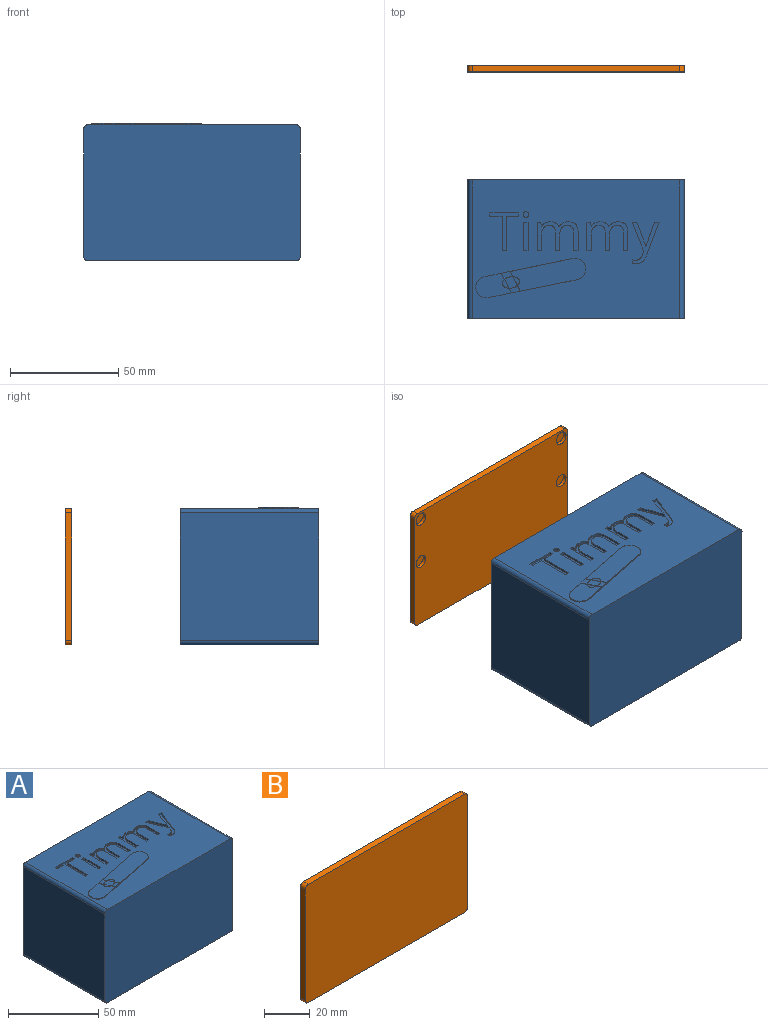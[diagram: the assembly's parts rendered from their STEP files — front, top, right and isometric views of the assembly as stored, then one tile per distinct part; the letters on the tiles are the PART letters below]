
ASSEMBLY  parts=2 mates=1
PART A: 152 faces, bbox 100x64x63.7 mm
  f0: plane 5.34x3.69mm, normal (0,0,1), area 10.9mm2, adj f140,f145,f146,f149
  f1: plane 96x64mm, normal (0,0,1), area 5297.7mm2, adj f2,f7,f37,f38,f39,f40,f41,f42
  f2: plane 100x63mm, normal (0,1,0), area 2285.3mm2, adj f1,f3,f4,f6,f8,f9,f10,f11
  f3: plane 47.5x22.2mm, normal (0,0,-1), area 1054.5mm2, adj f2,f5,f14,f18
  f4: plane 47.5x22.2mm, normal (0,0,1), area 1054.5mm2, adj f2,f5,f14,f18
  f5: cylinder r=15mm len=30mm, axis (1,0,0), area 1046.2mm2, adj f3,f4,f14,f18
  f6: plane 64x59mm, normal (-1,0,0), area 3776mm2, adj f2,f7,f135,f137
  f7: plane 100x63mm, normal (0,-1,0), area 6296.6mm2, adj f1,f6,f8,f9,f135,f136,f137,f138
  f8: plane 64x59mm, normal (1,0,0), area 3776mm2, adj f2,f7,f136,f138
  f9: plane 96x64mm, normal (0,0,-1), area 6144mm2, adj f2,f7,f135,f136
  f10: plane 62.5x30mm, normal (1,0,0), area 1778.4mm2, adj f2,f11,f12,f13
  f11: plane 66.5x47.5mm, normal (0,0,-1), area 3158.8mm2, adj f2,f10,f13,f16
  f12: plane 66.5x47.5mm, normal (0,0,1), area 3158.8mm2, adj f2,f10,f13,f16
  f13: cylinder r=15mm len=66.5mm, axis (1,0,0), area 3133.7mm2, adj f10,f11,f12,f16
  f14: plane 62.5x30mm, normal (-1,0,0), area 1778.4mm2, adj f2,f3,f4,f5
  f15: plane 63x7.8mm, normal (0,0,-1), area 491.4mm2, adj f2,f16,f18,f19
  f16: plane 63x32mm, normal (1,0,0), area 237.6mm2, adj f2,f11,f12,f13,f15,f17,f19
  f17: plane 63x7.8mm, normal (0,0,1), area 491.4mm2, adj f2,f16,f18,f19
  f18: plane 63x32mm, normal (-1,0,0), area 237.6mm2, adj f2,f3,f4,f5,f15,f17,f19
  f19: plane 32x7.8mm, normal (0,1,0), area 249.6mm2, adj f15,f16,f17,f18
  f20: plane 73x42mm, normal (0,0,1), area 2851mm2, adj f2,f21,f23,f24,f25,f27,f28
  f21: plane 42x13mm, normal (1,0,0), area 546mm2, adj f2,f20,f22,f24
  f22: plane 73x42mm, normal (0,0,-1), area 3066mm2, adj f2,f21,f23,f24
  f23: plane 42x13mm, normal (-1,0,0), area 546mm2, adj f2,f20,f22,f24
  f24: plane 73x13mm, normal (0,1,0), area 949mm2, adj f20,f21,f22,f23
  f25: plane 25x3mm, normal (-1,0,0), area 75mm2, adj f2,f20,f26,f28
  f26: plane 25x8.6mm, normal (0,0,1), area 215mm2, adj f2,f25,f27,f28
  f27: plane 25x3mm, normal (1,0,0), area 75mm2, adj f2,f20,f26,f28
  f28: plane 8.6x3mm, normal (0,1,0), area 25.8mm2, adj f20,f25,f26,f27
  f29: cylinder r=3.17mm len=6.33mm, axis (0,1,0), area 32mm2, adj f2,f30
  f30: plane 6.33x6.33mm, normal (0,1,0), area 31.5mm2, adj f29
  f31: cylinder r=3.17mm len=6.33mm, axis (0,1,0), area 32mm2, adj f2,f32
  f32: plane 6.33x6.33mm, normal (0,1,0), area 31.5mm2, adj f31
  f33: cylinder r=3.17mm len=6.33mm, axis (0,1,0), area 32mm2, adj f2,f34
  f34: plane 6.33x6.33mm, normal (0,1,0), area 31.5mm2, adj f33
  f35: cylinder r=3.17mm len=6.33mm, axis (0,1,0), area 32mm2, adj f2,f36
  f36: plane 6.33x6.33mm, normal (0,1,0), area 31.5mm2, adj f35
  f37: plane 2.15x1mm, normal (0,-1,0), area 2.2mm2, adj f1,f38,f52,f53
  f38: plane 13.31x5.34mm, normal (0.93,0.37,0), area 14.3mm2, adj f1,f37,f39,f53
  f39: plane 1.88x1mm, normal (0.93,-0.37,0), area 2mm2, adj f1,f38,f40,f53
  f40: extruded ~2.95x2.32mm, area 4mm2, adj f1,f39,f41,f53
  f41: extruded ~1.48x1mm, area 1.5mm2, adj f1,f40,f42,f53
  f42: plane 1.6x1mm, normal (1,0,0), area 1.6mm2, adj f1,f41,f43,f53
  f43: extruded ~1.81x1mm, area 1.8mm2, adj f1,f42,f44,f53
  f44: extruded ~2.77x1mm, area 3mm2, adj f1,f43,f45,f53
  f45: extruded ~3.17x1.98mm, area 3.8mm2, adj f1,f44,f46,f53
  f46: plane 15.07x5.69mm, normal (-0.94,0.35,0), area 16.1mm2, adj f1,f45,f47,f53
  f47: plane 2.15x1mm, normal (0,-1,0), area 2.1mm2, adj f1,f46,f48,f53
  f48: extruded ~9.17x3.28mm, area 9.7mm2, adj f1,f47,f49,f53
  f49: extruded ~2.11x1mm, area 2.2mm2, adj f1,f48,f50,f53
  f50: plane 1x0.1mm, normal (0,-1,0), area 0.1mm2, adj f1,f49,f51,f53
  f51: extruded ~3.73x1.18mm, area 3.9mm2, adj f1,f50,f52,f53
  f52: plane 7.55x2.9mm, normal (-0.93,-0.36,0), area 8.1mm2, adj f1,f37,f51,f53
  f53: plane 19.18x12.42mm, normal (0,0,1), area 68mm2, adj f37,f38,f39,f40,f41,f42,f43,f44
  f54: plane 8.61x1mm, normal (1,0,0), area 8.6mm2, adj f1,f55,f81,f82
  f55: plane 2x1mm, normal (0,1,0), area 2mm2, adj f1,f54,f56,f82
  f56: plane 8.63x1mm, normal (-1,0,0), area 8.6mm2, adj f1,f55,f57,f82
  f57: extruded ~3.69x1.12mm, area 4mm2, adj f1,f56,f58,f82
  f58: extruded ~3.36x1.15mm, area 3.7mm2, adj f1,f57,f59,f82
  f59: extruded ~2.56x1mm, area 2.7mm2, adj f1,f58,f60,f82
  f60: extruded ~1.71x1.64mm, area 2.4mm2, adj f1,f59,f61,f82
  f61: plane 1x0.1mm, normal (0,-1,0), area 0.1mm2, adj f1,f60,f62,f82
  f62: extruded ~4.06x2.25mm, area 5mm2, adj f1,f61,f63,f82
  f63: extruded ~2.31x1mm, area 2.4mm2, adj f1,f62,f64,f82
  f64: extruded ~1.6x1.51mm, area 2.2mm2, adj f1,f63,f65,f82
  f65: plane 1x0.1mm, normal (0,-1,0), area 0.1mm2, adj f1,f64,f66,f82
  f66: plane 1.81x1mm, normal (-0.98,-0.18,0), area 1.8mm2, adj f1,f65,f67,f82
  f67: plane 1.63x1mm, normal (0,-1,0), area 1.6mm2, adj f1,f66,f68,f82
  f68: plane 13.24x1mm, normal (1,0,0), area 13.2mm2, adj f1,f67,f69,f82
  f69: plane 2.01x1mm, normal (0,1,0), area 2mm2, adj f1,f68,f70,f82
  f70: plane 6.95x1mm, normal (-1,0,0), area 6.9mm2, adj f1,f69,f71,f82
  f71: extruded ~3.7x1mm, area 3.9mm2, adj f1,f70,f72,f82
  f72: extruded ~2.76x1.13mm, area 3.1mm2, adj f1,f71,f73,f82
  f73: extruded ~2.11x1mm, area 2.3mm2, adj f1,f72,f74,f82
  f74: extruded ~2.38x1mm, area 2.5mm2, adj f1,f73,f75,f82
  f75: plane 8.61x1mm, normal (1,0,0), area 8.6mm2, adj f1,f74,f76,f82
  f76: plane 2.01x1mm, normal (0,1,0), area 2mm2, adj f1,f75,f77,f82
  f77: plane 7.39x1mm, normal (-1,0,0), area 7.4mm2, adj f1,f76,f78,f82
  f78: extruded ~3.31x1mm, area 3.5mm2, adj f1,f77,f79,f82
  f79: extruded ~2.77x1.07mm, area 3.1mm2, adj f1,f78,f80,f82
  f80: extruded ~2.1x1mm, area 2.3mm2, adj f1,f79,f81,f82
  f81: extruded ~2.38x1mm, area 2.5mm2, adj f1,f54,f80,f82
  f82: plane 18.88x13.48mm, normal (0,0,1), area 99.3mm2, adj f54,f55,f56,f57,f58,f59,f60,f61
  f83: plane 8.61x1mm, normal (1,0,0), area 8.6mm2, adj f1,f84,f110,f111
  f84: plane 2x1mm, normal (0,1,0), area 2mm2, adj f1,f83,f85,f111
  f85: plane 8.63x1mm, normal (-1,0,0), area 8.6mm2, adj f1,f84,f86,f111
  f86: extruded ~3.69x1.12mm, area 4mm2, adj f1,f85,f87,f111
  f87: extruded ~3.36x1.15mm, area 3.7mm2, adj f1,f86,f88,f111
  f88: extruded ~2.56x1mm, area 2.7mm2, adj f1,f87,f89,f111
  f89: extruded ~1.71x1.64mm, area 2.4mm2, adj f1,f88,f90,f111
  f90: plane 1x0.1mm, normal (0,-1,0), area 0.1mm2, adj f1,f89,f91,f111
  f91: extruded ~4.06x2.25mm, area 5mm2, adj f1,f90,f92,f111
  f92: extruded ~2.31x1mm, area 2.4mm2, adj f1,f91,f93,f111
  f93: extruded ~1.6x1.51mm, area 2.2mm2, adj f1,f92,f94,f111
  f94: plane 1x0.1mm, normal (0,-1,0), area 0.1mm2, adj f1,f93,f95,f111
  f95: plane 1.81x1mm, normal (-0.98,-0.18,0), area 1.8mm2, adj f1,f94,f96,f111
  f96: plane 1.63x1mm, normal (0,-1,0), area 1.6mm2, adj f1,f95,f97,f111
  f97: plane 13.24x1mm, normal (1,0,0), area 13.2mm2, adj f1,f96,f98,f111
  f98: plane 2.01x1mm, normal (0,1,0), area 2mm2, adj f1,f97,f99,f111
  f99: plane 6.95x1mm, normal (-1,0,0), area 6.9mm2, adj f1,f98,f100,f111
  f100: extruded ~3.7x1mm, area 3.9mm2, adj f1,f99,f101,f111
  f101: extruded ~2.76x1.13mm, area 3.1mm2, adj f1,f100,f102,f111
  f102: extruded ~2.11x1mm, area 2.3mm2, adj f1,f101,f103,f111
  f103: extruded ~2.38x1mm, area 2.5mm2, adj f1,f102,f104,f111
  f104: plane 8.61x1mm, normal (1,0,0), area 8.6mm2, adj f1,f103,f105,f111
  f105: plane 2.01x1mm, normal (0,1,0), area 2mm2, adj f1,f104,f106,f111
  f106: plane 7.39x1mm, normal (-1,0,0), area 7.4mm2, adj f1,f105,f107,f111
  f107: extruded ~3.31x1mm, area 3.5mm2, adj f1,f106,f108,f111
  f108: extruded ~2.77x1.07mm, area 3.1mm2, adj f1,f107,f109,f111
  f109: extruded ~2.1x1mm, area 2.3mm2, adj f1,f108,f110,f111
  f110: extruded ~2.38x1mm, area 2.5mm2, adj f1,f83,f109,f111
  f111: plane 18.88x13.48mm, normal (0,0,1), area 99.3mm2, adj f83,f84,f85,f86,f87,f88,f89,f90
  f112: extruded ~1.01x1mm, area 1.1mm2, adj f1,f113,f119,f120
  f113: extruded ~1.01x1mm, area 1.1mm2, adj f1,f112,f114,f120
  f114: extruded ~1x0.85mm, area 0.9mm2, adj f1,f113,f115,f120
  f115: extruded ~1x0.83mm, area 0.9mm2, adj f1,f114,f116,f120
  f116: extruded ~1.01x1mm, area 1.1mm2, adj f1,f115,f117,f120
  f117: extruded ~1x1mm, area 1.1mm2, adj f1,f116,f118,f120
  f118: extruded ~1x0.83mm, area 0.9mm2, adj f1,f117,f119,f120
  f119: extruded ~1x0.85mm, area 0.9mm2, adj f1,f112,f118,f120
  f120: plane 2.67x2.37mm, normal (0,0,1), area 5.2mm2, adj f112,f113,f114,f115,f116,f117,f118,f119
  f121: plane 2.01x1mm, normal (0,1,0), area 2mm2, adj f1,f122,f124,f125
  f122: plane 13.24x1mm, normal (-1,0,0), area 13.2mm2, adj f1,f121,f123,f125
  f123: plane 2.01x1mm, normal (0,-1,0), area 2mm2, adj f1,f122,f124,f125
  f124: plane 13.24x1mm, normal (1,0,0), area 13.2mm2, adj f1,f121,f123,f125
  f125: plane 13.24x2.01mm, normal (0,0,1), area 26.6mm2, adj f121,f122,f123,f124
  f126: plane 2.05x1mm, normal (0,1,0), area 2.1mm2, adj f1,f127,f133,f134
  f127: plane 15.83x1mm, normal (-1,0,0), area 15.8mm2, adj f1,f126,f128,f134
  f128: plane 5.59x1mm, normal (0,1,0), area 5.6mm2, adj f1,f127,f129,f134
  f129: plane 1.82x1mm, normal (-1,0,0), area 1.8mm2, adj f1,f128,f130,f134
  f130: plane 13.24x1mm, normal (0,-1,0), area 13.2mm2, adj f1,f129,f131,f134
  f131: plane 1.82x1mm, normal (1,0,0), area 1.8mm2, adj f1,f130,f132,f134
  f132: plane 5.59x1mm, normal (0,1,0), area 5.6mm2, adj f1,f131,f133,f134
  f133: plane 15.83x1mm, normal (1,0,0), area 15.8mm2, adj f1,f126,f132,f134
  f134: plane 17.66x13.24mm, normal (0,0,1), area 56.6mm2, adj f126,f127,f128,f129,f130,f131,f132,f133
  f135: cylinder r=2mm len=64mm, axis (0,-1,0), area 201.1mm2, adj f2,f6,f7,f9
  f136: cylinder r=2mm len=64mm, axis (0,1,0), area 201.1mm2, adj f2,f7,f8,f9
  f137: cylinder r=2mm len=64mm, axis (0,1,0), area 201.1mm2, adj f1,f2,f6,f7
  f138: cylinder r=2mm len=64mm, axis (0,-1,0), area 201.1mm2, adj f1,f2,f7,f8
  f139: plane 39.89x8.05mm, normal (0.2,-0.98,0), area 20.8mm2, adj f1,f141,f142,f143,f144,f145,f146,f147
  f140: plane 39.83x8.24mm, normal (-0.2,0.98,0), area 20.8mm2, adj f0,f1,f141,f142,f143,f144,f145,f146
  f141: cylinder r=5mm len=10mm, axis (0,0,-1), area 8.8mm2, adj f1,f139,f140,f142
  f142: plane 16.54x11.41mm, normal (0,0,1), area 131.4mm2, adj f139,f140,f141,f145
  f143: cylinder r=5mm len=9.9mm, axis (0,0,-1), area 7.9mm2, adj f1,f139,f140,f144
  f144: plane 34.96x15.19mm, normal (0,0,1), area 318.9mm2, adj f139,f140,f143,f146
  f145: plane 9.08x4.73mm, normal (-0.89,-0.46,0), area 1mm2, adj f0,f139,f140,f142,f147,f148
  f146: plane 9.1x4.74mm, normal (0.89,0.46,0), area 1mm2, adj f0,f139,f140,f144,f147,f151
  f147: plane 5.2x3.45mm, normal (0,0,1), area 9.8mm2, adj f139,f145,f146,f149
  f148: plane 4.08x3.1mm, normal (0,0,-1), area 6.2mm2, adj f145,f149
  f149: extruded ~7.85x5.33mm, area 1mm2, adj f0,f147,f148,f150,f151
  f150: plane 7.86x5.35mm, normal (0,0,1), area 32.6mm2, adj f149
  f151: plane 4.04x3.04mm, normal (0,0,-1), area 6mm2, adj f146,f149
PART B: 18 faces, bbox 100x3x63 mm
  f0: plane 59x3mm, normal (1,0,0), area 177mm2, adj f4,f5,f14,f17
  f1: plane 96x3mm, normal (0,0,1), area 288mm2, adj f4,f5,f14,f15
  f2: plane 59x3mm, normal (-1,0,0), area 177mm2, adj f4,f5,f15,f16
  f3: plane 96x3mm, normal (0,0,-1), area 288mm2, adj f4,f5,f16,f17
  f4: plane 100x63mm, normal (0,-1,0), area 6296.6mm2, adj f0,f1,f2,f3,f14,f15,f16,f17
  f5: plane 100x63mm, normal (0,1,0), area 6170.7mm2, adj f0,f1,f2,f3,f6,f8,f10,f12
  f6: cylinder r=3.17mm len=6.33mm, axis (0,1,0), area 33.2mm2, adj f5,f7
  f7: plane 6.33x6.33mm, normal (0,1,0), area 31.5mm2, adj f6
  f8: cylinder r=3.17mm len=6.33mm, axis (0,1,0), area 33.2mm2, adj f5,f9
  f9: plane 6.33x6.33mm, normal (0,1,0), area 31.5mm2, adj f8
  f10: cylinder r=3.17mm len=6.33mm, axis (0,1,0), area 33.2mm2, adj f5,f11
  f11: plane 6.33x6.33mm, normal (0,1,0), area 31.5mm2, adj f10
  f12: cylinder r=3.17mm len=6.33mm, axis (0,1,0), area 33.2mm2, adj f5,f13
  f13: plane 6.33x6.33mm, normal (0,1,0), area 31.5mm2, adj f12
  f14: cylinder r=2mm len=3mm, axis (0,-1,0), area 9.4mm2, adj f0,f1,f4,f5
  f15: cylinder r=2mm len=3mm, axis (0,1,0), area 9.4mm2, adj f1,f2,f4,f5
  f16: cylinder r=2mm len=3mm, axis (0,-1,0), area 9.4mm2, adj f2,f3,f4,f5
  f17: cylinder r=2mm len=3mm, axis (0,1,0), area 9.4mm2, adj f0,f3,f4,f5
PLACE A rot(axis=(-0.15,0.99,0.03),0deg) t=(92.57,-108.24,-21.47)mm fixed
PLACE B rot(axis=(0,0,-1),180deg) t=(118.4,5.76,-21.47)mm
MATE slider A.f2 <-> B.f5  axis (0,1,0) through (42.57,-44.24,41.53)mm
